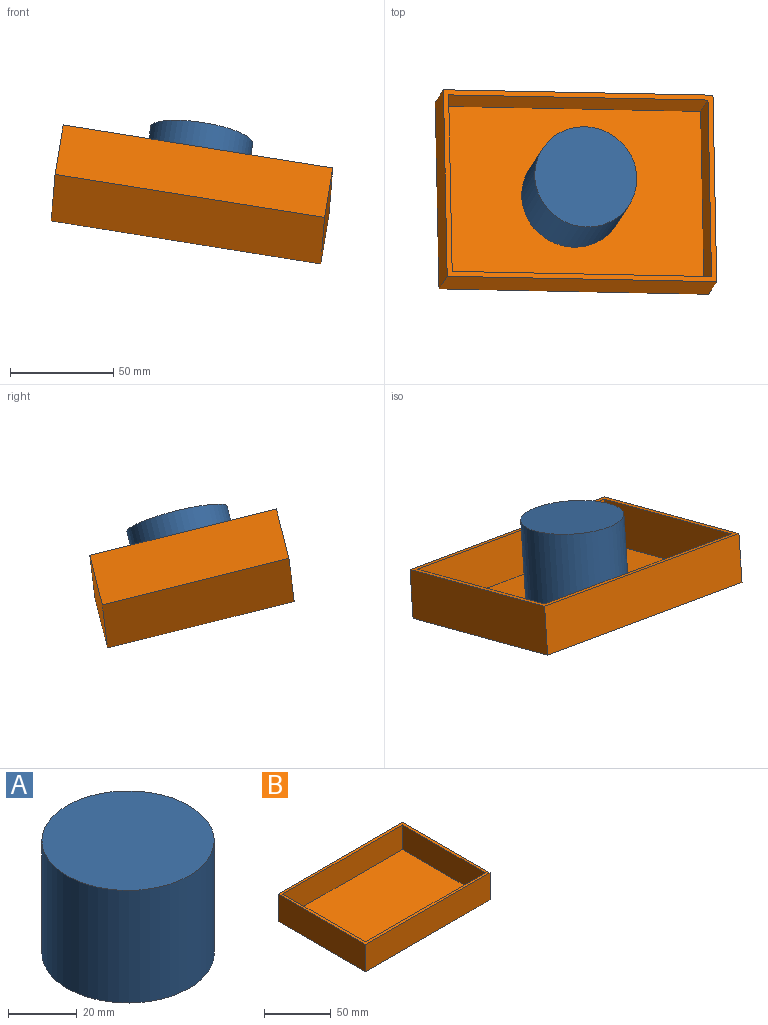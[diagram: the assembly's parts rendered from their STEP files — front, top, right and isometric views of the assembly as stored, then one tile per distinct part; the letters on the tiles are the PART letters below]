
ASSEMBLY  parts=2 mates=1
PART A: 3 faces, bbox 50x50x40 mm
  f0: cylinder r=25mm len=50mm, axis (0,0,-1), area 6283.2mm2, adj f1,f2
  f1: plane 50x50mm, normal (0,0,1), area 1963.5mm2, adj f0
  f2: plane 50x50mm, normal (0,0,-1), area 1963.5mm2, adj f0
PART B: 11 faces, bbox 132x93x25 mm
  f0: plane 132.02x93.01mm, normal (0,0,1), area 1100.2mm2, adj f1,f2,f3,f4,f6,f7,f8,f9
  f1: plane 132.02x25mm, normal (0,-1,0), area 3300.5mm2, adj f0,f2,f4,f5
  f2: plane 93.01x25mm, normal (1,0,0), area 2325.3mm2, adj f0,f1,f3,f5
  f3: plane 132.02x25mm, normal (0,1,0), area 3300.5mm2, adj f0,f2,f4,f5
  f4: plane 93.01x25mm, normal (-1,0,0), area 2325.3mm2, adj f0,f1,f3,f5
  f5: plane 132.02x93.01mm, normal (0,0,-1), area 12279.5mm2, adj f1,f2,f3,f4
  f6: plane 127.02x22.5mm, normal (0,1,0), area 2858mm2, adj f0,f7,f9,f10
  f7: plane 88.01x22.5mm, normal (-1,0,0), area 1980.3mm2, adj f0,f6,f8,f10
  f8: plane 127.02x22.5mm, normal (0,-1,0), area 2858mm2, adj f0,f7,f9,f10
  f9: plane 88.01x22.5mm, normal (1,0,0), area 1980.3mm2, adj f0,f6,f8,f10
  f10: plane 127.02x88.01mm, normal (0,0,1), area 11179.4mm2, adj f6,f7,f8,f9
PLACE A rot(axis=(-0.81,0.47,-0.35),17.9deg) t=(-28.17,62.94,2.94)mm
PLACE B rot(axis=(-0.84,0.55,0),16.8deg) t=(-28.57,62.34,0.54)mm
MATE planar A.f0 <-> B.f10  axis (-0.16,-0.24,-0.96) through (-28.17,62.94,2.94)mm
